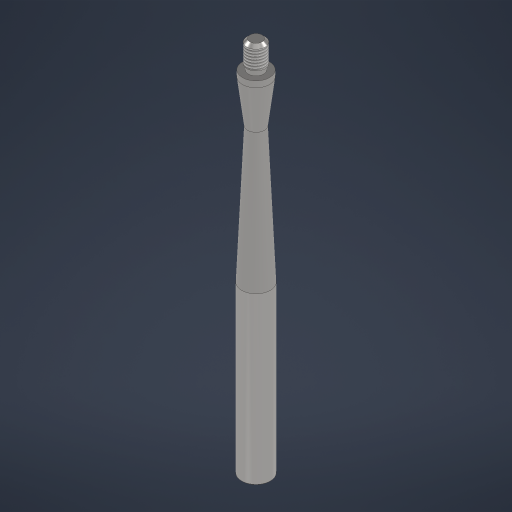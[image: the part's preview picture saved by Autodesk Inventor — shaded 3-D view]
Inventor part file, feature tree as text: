
AUTODESK INVENTOR PART (.ipt)
format: ipt  version: 2024.3 (Build 283343000, 343)  size: 231,424 bytes
history: native  units: mm
features: chamfer x2, sketch x2, revolve x1, thread x1, hole x1, other x1
ambient origin geometry x8: Origin, YZ Plane, XZ Plane, XY Plane, X Axis, Y Axis, Z Axis, Center Point
bodies: Solid1 (feature_tree)
feature tree (8):
  revolve  "Revolution1"  [1 undecoded]
  thread  "Thread1"  [1 undecoded]
  hole  "Hole1"  [1 undecoded]
  chamfer  "Chamfer2"  Distance=3.0mm
  chamfer  "Chamfer3"  Distance=18.0mm
  sketch  "Sketch1"  dims[d0=250.0mm d1=19.0mm d2=110.0mm]
  sketch  "Sketch2"  dims[d5=11.14103mm d6=12.0mm d7=3.0mm d9=18.0mm d10=4.0mm d11=10.0mm d12=60.0deg d13=18.0mm d14=0.436332mm d15=90.0deg d16=1.218746mm d17=200.0mm d18=232.0mm d19=50.0mm d20=14.42265mm d21=13.268mm d22=0.0mm d23=15.0mm d24=0.5mm d25=15.5mm d26=2.0mm d27=90.0deg d28=80.0mm d29=20.594885mm d41=2.0mm d42=2.0mm d43=45.0deg d44=0.5mm d45=2.0mm d46=45.0deg]
  other  "Finish1"
note: 3 required parameter values undecoded (feature->parameter linkage not recoverable at this tier; creation-order binding heuristic only, values carry confidence <= 0.55)